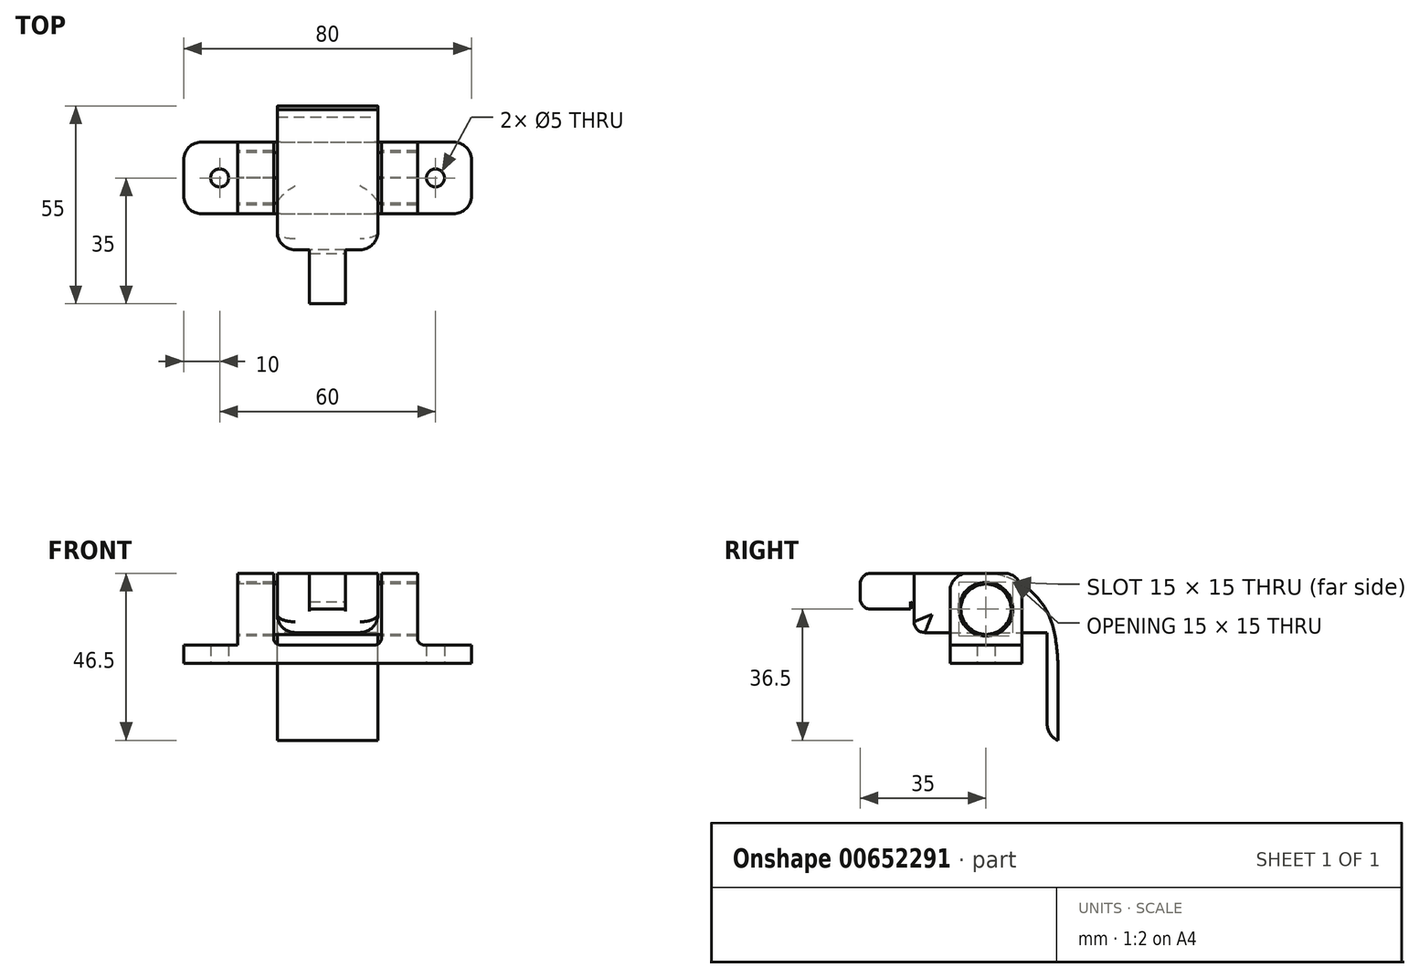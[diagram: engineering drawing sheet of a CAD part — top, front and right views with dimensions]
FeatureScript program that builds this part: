
annotation { "Feature Type Name" : "Feature", "Feature Type Description" : "" }
export const myFeature = defineFeature(function(context is Context, id is Id, definition is map)
    precondition{}
    {
        {
            var Q0;
            Q0=qCreatedBy(makeId("Top.planeOp"),FACE);
            var sketch = newSketch(context, id + "F0", { "sketchPlane" : qUnion([Q0])});
            skLineSegment(sketch, "E0.bottom", {"start": v(-40, -10) * mm, "end": v(40, -10) * mm});
            skLineSegment(sketch, "E0.top", {"start": v(-40, 10) * mm, "end": v(40, 10) * mm});
            skLineSegment(sketch, "E0.left", {"start": v(-40, -10) * mm, "end": v(-40, 10) * mm});
            skLineSegment(sketch, "E0.right", {"start": v(40, -10) * mm, "end": v(40, 10) * mm});
            skCircle(sketch, "E1", {"center": v(-30, 0) * mm, "radius": 2.5 * mm});
            skCircle(sketch, "E2.MirrorC", {"center": v(30, 0) * mm, "radius": 2.5 * mm});
            skSolve(sketch);
        }
        {
            var Q0;
            Q0=makeQuery(id+"F0.imprint","IMPRINT",FACE,{"disambiguationData":[TD([[makeQuery(id+"F0.imprint","IMPRINT",EDGE,{"derivedFrom":sQuery(id+"F0.wireOp",EDGE,"E0.bottom")}),1.0]])]});
            extrude(context, id + "F1", {"entities" : qUnion([Q0]), "depth" : 5 * mm, "offsetDistance" : 25 * mm});
        }
        {
            var Q0;
            Q0=makeQuery(id+"F1.opExtrude","CAP_FACE",FACE,{"disambiguationData":[OSD([sQuery(id+"F0.wireOp",EDGE,"E0.bottom"),sQuery(id+"F0.wireOp",EDGE,"E0.top"),sQuery(id+"F0.wireOp",EDGE,"E0.left"),sQuery(id+"F0.wireOp",EDGE,"E0.right"),sQuery(id+"F0.wireOp",EDGE,"E1"),sQuery(id+"F0.wireOp",EDGE,"E2.MirrorC")])],"isStart":false});
            var sketch = newSketch(context, id + "F2", { "sketchPlane" : qUnion([Q0])});
            skLineSegment(sketch, "E3.bottom", {"start": v(-25, 10) * mm, "end": v(-15, 10) * mm});
            skLineSegment(sketch, "E3.top", {"start": v(-25, -10) * mm, "end": v(-15, -10) * mm});
            skLineSegment(sketch, "E3.left", {"start": v(-25, 10) * mm, "end": v(-25, -10) * mm});
            skLineSegment(sketch, "E3.right", {"start": v(-15, 10) * mm, "end": v(-15, -10) * mm});
            skLineSegment(sketch, "E4.MirrorCS", {"start": v(15, 10) * mm, "end": v(15, -10) * mm});
            skLineSegment(sketch, "E5.MirrorCS", {"start": v(25, 10) * mm, "end": v(25, -10) * mm});
            skLineSegment(sketch, "E6", {"start": v(15, 10) * mm, "end": v(25, 10) * mm});
            skLineSegment(sketch, "E7", {"start": v(15, -10) * mm, "end": v(25, -10) * mm});
            skSolve(sketch);
        }
        {
            var Q0;
            Q0=makeQuery(id+"F2.imprint","IMPRINT",FACE,{"disambiguationData":[TD([[makeQuery(id+"F2.imprint","IMPRINT",EDGE,{"derivedFrom":sQuery(id+"F2.wireOp",EDGE,"E3.bottom")}),-1.0]])]});
            var Q1;
            Q1=makeQuery(id+"F2.imprint","IMPRINT",FACE,{"disambiguationData":[TD([[makeQuery(id+"F2.imprint","IMPRINT",EDGE,{"derivedFrom":sQuery(id+"F2.wireOp",EDGE,"E4.MirrorCS")}),1.0]])]});
            extrude(context, id + "F3", {"entities" : qUnion([Q0, Q1]), "operationType" : NewBodyOperationType.ADD, "depth" : 20 * mm, "offsetDistance" : 25 * mm});
        }
        {
            var Q0;
            Q0=makeQuery(id+"F3.opExtrude","SWEPT_FACE",FACE,{"disambiguationData":[OSD([sQuery(id+"F2.wireOp",EDGE,"E3.left")])]});
            var sketch = newSketch(context, id + "F4", { "sketchPlane" : qUnion([Q0])});
            skCircle(sketch, "E8", {"center": v(0, 15) * mm, "radius": 7.5 * mm});
            skSolve(sketch);
        }
        {
            var Q0;
            Q0=makeQuery(id+"F4.imprint","IMPRINT",FACE,{"disambiguationData":[TD([[makeQuery(id+"F4.imprint","IMPRINT",EDGE,{"derivedFrom":sQuery(id+"F4.wireOp",EDGE,"E8")}),1.0]])]});
            extrude(context, id + "F5", {"entities" : qUnion([Q0]), "operationType" : NewBodyOperationType.REMOVE, "oppositeDirection" : true, "depth" : 50 * mm, "offsetDistance" : 25 * mm});
        }
        {
            var Q0;
            Q0=makeQuery(id+"F1.opExtrude","SWEPT_EDGE",EDGE,{"disambiguationData":[OSD([sQuery(id+"F0.wireOp",EDGE,"E0.bottom"),sQuery(id+"F0.wireOp",EDGE,"E0.right")])]});
            var Q1;
            Q1=makeQuery(id+"F1.opExtrude","SWEPT_EDGE",EDGE,{"disambiguationData":[OSD([sQuery(id+"F0.wireOp",EDGE,"E0.top"),sQuery(id+"F0.wireOp",EDGE,"E0.right")])]});
            var Q2;
            Q2=makeQuery(id+"F1.opExtrude","SWEPT_EDGE",EDGE,{"disambiguationData":[OSD([sQuery(id+"F0.wireOp",EDGE,"E0.bottom"),sQuery(id+"F0.wireOp",EDGE,"E0.left")])]});
            var Q3;
            Q3=makeQuery(id+"F1.opExtrude","SWEPT_EDGE",EDGE,{"disambiguationData":[OSD([sQuery(id+"F0.wireOp",EDGE,"E0.top"),sQuery(id+"F0.wireOp",EDGE,"E0.left")])]});
            var Q4;
            Q4=makeQuery(id+"F3.opExtrude","CAP_EDGE",EDGE,{"disambiguationData":[OSD([sQuery(id+"F2.wireOp",EDGE,"E3.bottom")])],"isStart":false});
            var Q5;
            Q5=makeQuery(id+"F3.opExtrude","CAP_EDGE",EDGE,{"disambiguationData":[OSD([sQuery(id+"F2.wireOp",EDGE,"E3.top")])],"isStart":false});
            var Q6;
            Q6=makeQuery(id+"F3.opExtrude","CAP_EDGE",EDGE,{"disambiguationData":[OSD([sQuery(id+"F2.wireOp",EDGE,"E7")])],"isStart":false});
            var Q7;
            Q7=makeQuery(id+"F3.opExtrude","CAP_EDGE",EDGE,{"disambiguationData":[OSD([sQuery(id+"F2.wireOp",EDGE,"E6")])],"isStart":false});
            fillet(context, id + "F6", {"entities" : qUnion([Q0, Q1, Q2, Q3, Q4, Q5, Q6, Q7]), "radius" : 5 * mm, "tangentPropagation" : true, "allowEdgeOverflow" : false});
        }
        {
            var Q0;
            Q0=makeQuery(id+"F3.opExtrude","CAP_EDGE",EDGE,{"disambiguationData":[OSD([sQuery(id+"F2.wireOp",EDGE,"E3.right")])],"isStart":true});
            var Q1;
            Q1=makeQuery(id+"F3.opExtrude","CAP_EDGE",EDGE,{"disambiguationData":[OSD([sQuery(id+"F2.wireOp",EDGE,"E3.left")])],"isStart":true});
            var Q2;
            Q2=makeQuery(id+"F3.opExtrude","CAP_EDGE",EDGE,{"disambiguationData":[OSD([sQuery(id+"F2.wireOp",EDGE,"E5.MirrorCS")])],"isStart":true});
            var Q3;
            Q3=makeQuery(id+"F3.opExtrude","CAP_EDGE",EDGE,{"disambiguationData":[OSD([sQuery(id+"F2.wireOp",EDGE,"E4.MirrorCS")])],"isStart":true});
            fillet(context, id + "F7", {"entities" : qUnion([Q0, Q1, Q2, Q3]), "radius" : 2 * mm, "tangentPropagation" : true, "allowEdgeOverflow" : false});
        }
        {
            var Q0;
            Q0=makeQuery(id+"F3.opExtrude","SWEPT_FACE",FACE,{"disambiguationData":[OSD([sQuery(id+"F2.wireOp",EDGE,"E3.left")])]});
            var sketch = newSketch(context, id + "F8", { "sketchPlane" : qUnion([Q0])});
            skArc(sketch, "E9", {"start": v(-0.1, 22) * mm, "mid": v(0, 8) * mm, "end": v(0.1, 22) * mm});
            skLineSegment(sketch, "E10", {"start": v(-0.1, 22.5) * mm, "end": v(-0.1, 22) * mm});
            skLineSegment(sketch, "E11.MirrorCS", {"start": v(0.1, 22.5) * mm, "end": v(0.1, 22) * mm});
            skSolve(sketch);
        }
        {
            var Q0;
            Q0=makeQuery(id+"F8.imprint","IMPRINT",FACE,{"disambiguationData":[TD([[makeQuery(id+"F8.imprint","IMPRINT",EDGE,{"derivedFrom":sQuery(id+"F8.wireOp",EDGE,"E9")}),1.0]])]});
            extrude(context, id + "F9", {"entities" : qUnion([Q0]), "operationType" : NewBodyOperationType.ADD, "oppositeDirection" : true, "depth" : 50 * mm, "offsetDistance" : 25 * mm});
        }
        {
            var Q0;
            Q0=qCreatedBy(makeId("Front.planeOp"),FACE);
            var sketch = newSketch(context, id + "F10", { "sketchPlane" : qUnion([Q0])});
            skLineSegment(sketch, "E12.bottom", {"start": v(-14, 25) * mm, "end": v(14, 25) * mm});
            skLineSegment(sketch, "E12.top", {"start": v(-14, 8.5) * mm, "end": v(14, 8.5) * mm});
            skLineSegment(sketch, "E12.left", {"start": v(-14, 25) * mm, "end": v(-14, 8.5) * mm});
            skLineSegment(sketch, "E12.right", {"start": v(14, 25) * mm, "end": v(14, 8.5) * mm});
            skSolve(sketch);
        }
        {
            var Q0;
            Q0=makeQuery(id+"F10.imprint","IMPRINT",FACE,{"disambiguationData":[TD([[makeQuery(id+"F10.imprint","IMPRINT",EDGE,{"derivedFrom":sQuery(id+"F10.wireOp",EDGE,"E12.bottom")}),-1.0]])]});
            extrude(context, id + "F11", {"entities" : qUnion([Q0]), "operationType" : NewBodyOperationType.ADD, "depth" : 20 * mm, "offsetDistance" : 25 * mm, "hasSecondDirection" : true, "secondDirectionOppositeDirection" : true, "secondDirectionDepth" : 19 * mm});
        }
        {
            var Q0;
            Q0=makeQuery(id+"F11.opExtrude","CAP_FACE",FACE,{"disambiguationData":[OSD([sQuery(id+"F10.wireOp",EDGE,"E12.bottom"),sQuery(id+"F10.wireOp",EDGE,"E12.top"),sQuery(id+"F10.wireOp",EDGE,"E12.left"),sQuery(id+"F10.wireOp",EDGE,"E12.right")])],"isStart":false});
            var sketch = newSketch(context, id + "F12", { "sketchPlane" : qUnion([Q0])});
            skLineSegment(sketch, "E13.bottom", {"start": v(-5, 25) * mm, "end": v(5, 25) * mm});
            skLineSegment(sketch, "E13.top", {"start": v(-5, 15) * mm, "end": v(5, 15) * mm});
            skLineSegment(sketch, "E13.left", {"start": v(-5, 25) * mm, "end": v(-5, 15) * mm});
            skLineSegment(sketch, "E13.right", {"start": v(5, 25) * mm, "end": v(5, 15) * mm});
            skSolve(sketch);
        }
        {
            var Q0;
            Q0=makeQuery(id+"F12.imprint","IMPRINT",FACE,{"disambiguationData":[TD([[makeQuery(id+"F12.imprint","IMPRINT",EDGE,{"derivedFrom":sQuery(id+"F12.wireOp",EDGE,"E13.bottom")}),-1.0]])]});
            extrude(context, id + "F13", {"entities" : qUnion([Q0]), "operationType" : NewBodyOperationType.ADD, "depth" : 15 * mm, "offsetDistance" : 25 * mm});
        }
        {
            var Q0;
            Q0=makeQuery(id+"F11.opExtrude","SWEPT_FACE",FACE,{"disambiguationData":[OSD([sQuery(id+"F10.wireOp",EDGE,"E12.top")])]});
            var sketch = newSketch(context, id + "F14", { "sketchPlane" : qUnion([Q0])});
            skLineSegment(sketch, "E14.top", {"start": v(-14, -17) * mm, "end": v(14, -17) * mm});
            skLineSegment(sketch, "E15", {"start": v(-14, -17) * mm, "end": v(-14, -20) * mm});
            skLineSegment(sketch, "E16", {"start": v(-14, -20) * mm, "end": v(14, -20) * mm});
            skLineSegment(sketch, "E17", {"start": v(14, -20) * mm, "end": v(14, -17) * mm});
            skSolve(sketch);
        }
        {
            var Q0;
            {var subQ0=sQuery(id+"F14.wireOp",EDGE,"E14.top");Q0=makeQuery(id+"F14.imprint","IMPRINT",FACE,{"disambiguationData":[TD([[makeQuery(id+"F14.imprint","IMPRINT",EDGE,{"derivedFrom":subQ0}),-1.0]])]});}
            var Q1;
            {var subQ2=sQuery(id+"F14.wireOp",EDGE,"E16");Q1=makeQuery(id+"F14.imprint","IMPRINT",FACE,{"disambiguationData":[TD([[makeQuery(id+"F14.imprint","IMPRINT",EDGE,{"derivedFrom":subQ2}),1.0]])]});}
            extrude(context, id + "F15", {"entities" : qUnion([Q0, Q1]), "operationType" : NewBodyOperationType.ADD, "depth" : 30 * mm, "offsetDistance" : 25 * mm});
        }
        {
            var Q0;
            Q0=makeQuery(id+"F11.opExtrude","CAP_EDGE",EDGE,{"disambiguationData":[OSD([sQuery(id+"F10.wireOp",EDGE,"E12.top")])],"isStart":false});
            var Q1;
            Q1=makeQuery(id+"F13.opExtrude","CAP_EDGE",EDGE,{"disambiguationData":[OSD([sQuery(id+"F12.wireOp",EDGE,"E13.top")])],"isStart":false});
            var Q2;
            Q2=makeQuery(id+"F13.opExtrude","CAP_EDGE",EDGE,{"disambiguationData":[OSD([sQuery(id+"F12.wireOp",EDGE,"E13.bottom")])],"isStart":false});
            var Q3;
            Q3=makeQuery(id+"F11.boolean.opBoolean","INTERSECT",EDGE,{"disambiguationData":[OD(1.0)],"derivedFrom":[makeQuery(id+"F9.opExtrude","SWEPT_FACE",FACE,{"disambiguationData":[OSD([sQuery(id+"F8.wireOp",EDGE,"E9")])]}),makeQuery(id+"F11.opExtrude","SWEPT_FACE",FACE,{"disambiguationData":[OSD([sQuery(id+"F10.wireOp",EDGE,"E12.top")])]})]});
            var Q4;
            Q4=makeQuery(id+"F11.boolean.opBoolean","INTERSECT",EDGE,{"disambiguationData":[OD(0.0)],"derivedFrom":[makeQuery(id+"F9.opExtrude","SWEPT_FACE",FACE,{"disambiguationData":[OSD([sQuery(id+"F8.wireOp",EDGE,"E9")])]}),makeQuery(id+"F11.opExtrude","SWEPT_FACE",FACE,{"disambiguationData":[OSD([sQuery(id+"F10.wireOp",EDGE,"E12.top")])]})]});
            var Q5;
            Q5=makeQuery(id+"F15.opExtrude","CAP_EDGE",EDGE,{"disambiguationData":[OSD([sQuery(id+"F14.wireOp",EDGE,"E14.bottom")])],"isStart":false});
            fillet(context, id + "F16", {"entities" : qUnion([Q0, Q1, Q2, Q3, Q4, Q5]), "radius" : 3 * mm, "tangentPropagation" : true, "allowEdgeOverflow" : false});
        }
        {
            var Q0;
            Q0=makeQuery(id+"F13.opExtrude","SWEPT_FACE",FACE,{"disambiguationData":[OSD([sQuery(id+"F12.wireOp",EDGE,"E13.top")])]});
            var sketch = newSketch(context, id + "F17", { "sketchPlane" : qUnion([Q0])});
            skLineSegment(sketch, "E18.bottom", {"start": v(-5, 20) * mm, "end": v(5, 20) * mm});
            skLineSegment(sketch, "E18.top", {"start": v(-5, 21) * mm, "end": v(5, 21) * mm});
            skLineSegment(sketch, "E18.left", {"start": v(-5, 20) * mm, "end": v(-5, 21) * mm});
            skLineSegment(sketch, "E18.right", {"start": v(5, 20) * mm, "end": v(5, 21) * mm});
            skSolve(sketch);
        }
        {
            var Q0;
            Q0=makeQuery(id+"F17.imprint","IMPRINT",FACE,{"disambiguationData":[TD([[makeQuery(id+"F17.imprint","IMPRINT",EDGE,{"derivedFrom":sQuery(id+"F17.wireOp",EDGE,"E18.bottom")}),1.0]])]});
            extrude(context, id + "F18", {"entities" : qUnion([Q0]), "operationType" : NewBodyOperationType.REMOVE, "oppositeDirection" : true, "depth" : 2.1 * mm, "offsetDistance" : 25 * mm});
        }
        {
            var Q0;
            Q0=makeQuery(id+"F18.boolean.opBoolean","COPY",EDGE,{"derivedFrom":makeQuery(id+"F18.opExtrude","CAP_EDGE",EDGE,{"disambiguationData":[OSD([sQuery(id+"F17.wireOp",EDGE,"E18.top")])],"isStart":true})});
            var Q1;
            Q1=makeQuery(id+"F11.opExtrude","CAP_EDGE",EDGE,{"disambiguationData":[OSD([sQuery(id+"F10.wireOp",EDGE,"E12.right")])],"isStart":false});
            var Q2;
            Q2=makeQuery(id+"F11.opExtrude","CAP_EDGE",EDGE,{"disambiguationData":[OSD([sQuery(id+"F10.wireOp",EDGE,"E12.left")])],"isStart":false});
            fillet(context, id + "F19", {"entities" : qUnion([Q0, Q1, Q2]), "radius" : 5 * mm, "tangentPropagation" : true, "allowEdgeOverflow" : false});
        }
        {
            var Q0;
            Q0=makeQuery(id+"F18.boolean.opBoolean","COPY",EDGE,{"derivedFrom":makeQuery(id+"F18.opExtrude","CAP_EDGE",EDGE,{"disambiguationData":[OSD([sQuery(id+"F17.wireOp",EDGE,"E18.bottom")])],"isStart":false})});
            var Q1;
            Q1=makeQuery(id+"F13.opExtrude","CAP_EDGE",EDGE,{"disambiguationData":[OSD([sQuery(id+"F12.wireOp",EDGE,"E13.right")])],"isStart":true});
            var Q2;
            Q2=makeQuery(id+"F13.opExtrude","CAP_EDGE",EDGE,{"disambiguationData":[OSD([sQuery(id+"F12.wireOp",EDGE,"E13.left")])],"isStart":true});
            var Q3;
            Q3=makeQuery(id+"F15.opExtrude","CAP_EDGE",EDGE,{"disambiguationData":[OSD([sQuery(id+"F14.wireOp",EDGE,"E14.top")])],"isStart":true});
            fillet(context, id + "F20", {"entities" : qUnion([Q0, Q1, Q2, Q3]), "radius" : 4 * mm, "tangentPropagation" : true, "allowEdgeOverflow" : false});
        }
        {
            var Q0;
            Q0=makeQuery(id+"F11.opExtrude","CAP_EDGE",EDGE,{"disambiguationData":[OSD([sQuery(id+"F10.wireOp",EDGE,"E12.bottom")])],"isStart":true});
            fillet(context, id + "F21", {"entities" : qUnion([Q0]), "radius" : 20 * mm, "tangentPropagation" : true, "allowEdgeOverflow" : false});
        }
        {
            var Q0;
            Q0=makeQuery(id+"F15.opExtrude","CAP_EDGE",EDGE,{"disambiguationData":[OSD([sQuery(id+"F14.wireOp",EDGE,"E16")])],"isStart":true});
            fillet(context, id + "F22", {"entities" : qUnion([Q0]), "radius" : 50 * mm, "tangentPropagation" : true, "allowEdgeOverflow" : false});
        }
        {
            var Q0;
            Q0=makeQuery(id+"F22.opFillet","BLEND_EDGE",EDGE,{"blendedFrom":[makeQuery(id+"FNTxYydUeTcVARH_1.boolean.opBoolean","COPY",EDGE,{"derivedFrom":makeQuery(id+"FNTxYydUeTcVARH_1.opExtrude","CAP_EDGE",EDGE,{"disambiguationData":[OSD([sQuery(id+"FCrTPnlOTsiHXDj_1.wireOp",EDGE,"xyyMS0VC-HBF4-Op6K-Zja1-fc6qJn1ykl90.top")])],"isStart":false})}),makeQuery(id+"F15.opExtrude","SWEPT_FACE",FACE,{"disambiguationData":[OSD([sQuery(id+"F14.wireOp",EDGE,"E16")])]})],"blendedInto":[makeQuery(id+"F15.opExtrude","SWEPT_FACE",FACE,{"disambiguationData":[OSD([sQuery(id+"F14.wireOp",EDGE,"E16")])]})]});
            var Q1;
            Q1=makeQuery(id+"F15.opExtrude","CAP_EDGE",EDGE,{"disambiguationData":[OSD([sQuery(id+"F14.wireOp",EDGE,"E14.top")])],"isStart":false});
            fillet(context, id + "F23", {"entities" : qUnion([Q0, Q1]), "radius" : 5 * mm, "tangentPropagation" : true, "allowEdgeOverflow" : false});
        }
    });
